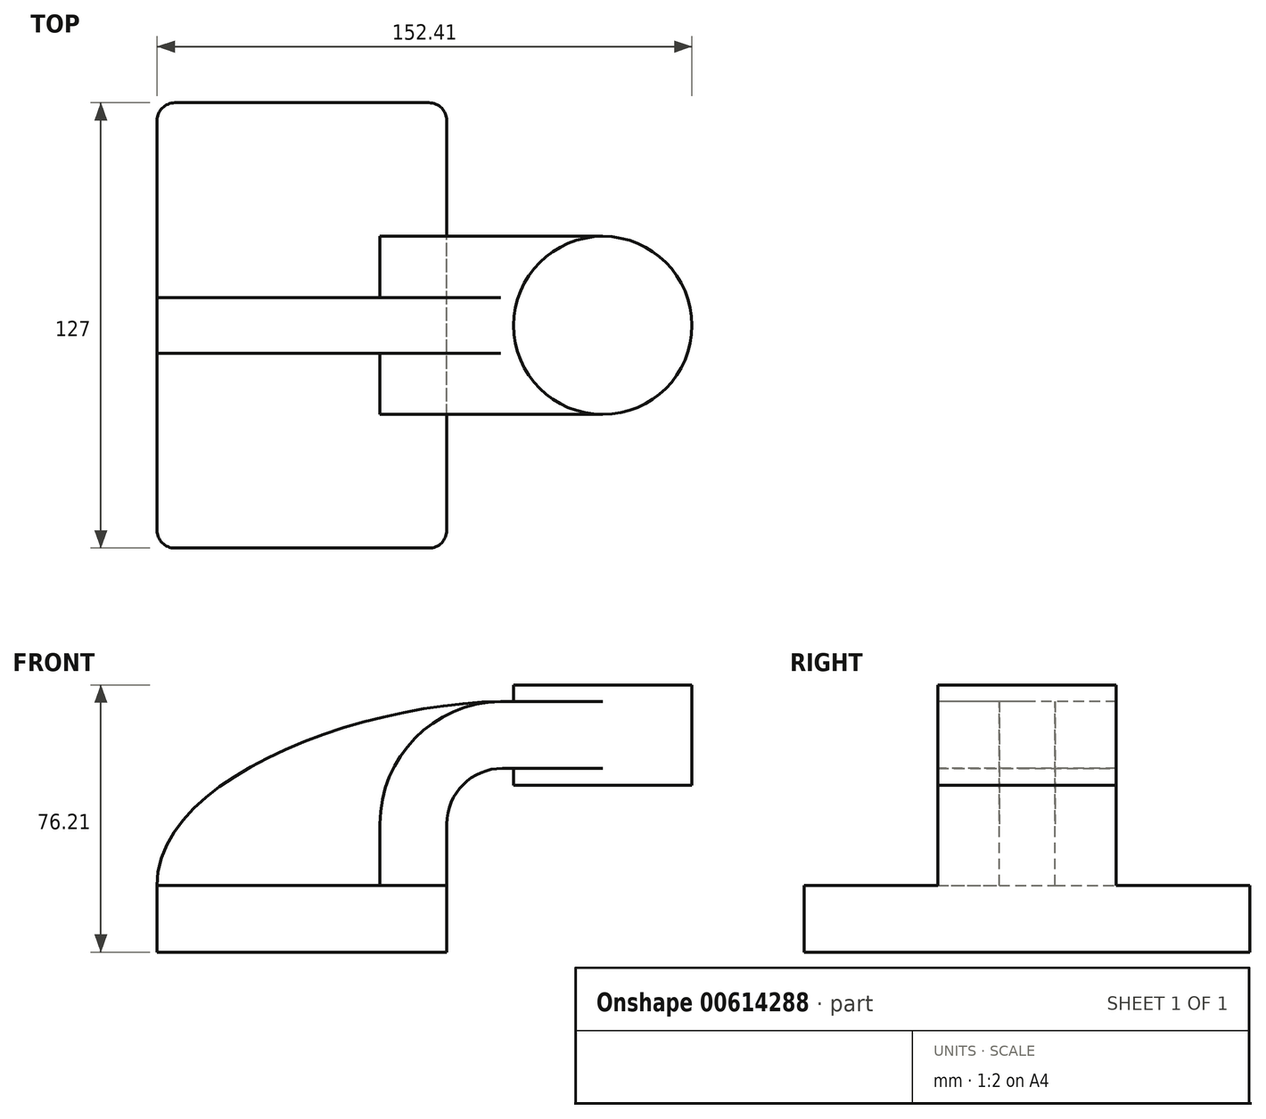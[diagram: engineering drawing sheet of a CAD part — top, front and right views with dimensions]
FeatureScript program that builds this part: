
annotation { "Feature Type Name" : "Feature", "Feature Type Description" : "" }
export const myFeature = defineFeature(function(context is Context, id is Id, definition is map)
    precondition{}
    {
        {
            var Q0;
            Q0=qCreatedBy(makeId("Front.planeOp"),FACE);
            var sketch = newSketch(context, id + "F0", { "sketchPlane" : qUnion([Q0])});
            skLineSegment(sketch, "E0.bottom", {"start": v(-41.28, 9.52) * mm, "end": v(41.27, 9.53) * mm});
            skLineSegment(sketch, "E0.top", {"start": v(-41.27, -9.53) * mm, "end": v(41.28, -9.53) * mm});
            skLineSegment(sketch, "E0.left", {"start": v(-41.28, 9.52) * mm, "end": v(-41.27, -9.53) * mm});
            skLineSegment(sketch, "E0.right", {"start": v(41.28, 9.53) * mm, "end": v(41.28, -9.52) * mm});
            skPoint(sketch, "E0.middle", {"position": v(0, 0) * mm});
            skLineSegment(sketch, "E1.bottom", {"start": v(60.32, 38.1) * mm, "end": v(111.12, 38.1) * mm});
            skLineSegment(sketch, "E1.top", {"start": v(60.32, 66.67) * mm, "end": v(111.12, 66.67) * mm});
            skLineSegment(sketch, "E1.left", {"start": v(60.32, 38.1) * mm, "end": v(60.32, 66.68) * mm});
            skLineSegment(sketch, "E1.right", {"start": v(111.12, 38.1) * mm, "end": v(111.12, 66.68) * mm});
            skPoint(sketch, "E1.middle", {"position": v(85.72, 52.39) * mm});
            skLineSegment(sketch, "E2", {"start": v(41.28, 9.53) * mm, "end": v(41.28, 27) * mm});
            skLineSegment(sketch, "E3", {"start": v(85.72, 38.1) * mm, "end": v(85.72, 66.67) * mm});
            skArc(sketch, "E4", {"start": v(41.27, 27) * mm, "mid": v(45.92, 38.23) * mm, "end": v(57.15, 42.88) * mm});
            skLineSegment(sketch, "E5", {"start": v(57.15, 42.88) * mm, "end": v(85.72, 42.88) * mm});
            skLineSegment(sketch, "E6.0", {"start": v(57.15, 61.93) * mm, "end": v(85.72, 61.93) * mm});
            skArc(sketch, "E6.1", {"start": v(22.23, 27) * mm, "mid": v(32.45, 51.7) * mm, "end": v(57.15, 61.93) * mm});
            skLineSegment(sketch, "E6.2", {"start": v(22.22, 9.53) * mm, "end": v(22.22, 27) * mm});
            skFitSpline(sketch, "E7", {"points": [v(-41.28, 9.52) * mm, v(57.15, 61.93) * mm], "startDerivative": vector(-1.16, 92.37) * mm, "endDerivative": vector(118.25, 0.68) * mm});
            skSolve(sketch);
        }
        {
            var Q0;
            Q0=makeQuery(id+"F0.imprint","IMPRINT",FACE,{"disambiguationData":[TD([[makeQuery(id+"F0.imprint","IMPRINT",EDGE,{"derivedFrom":sQuery(id+"F0.wireOp",EDGE,"E0.top")}),1.0]])]});
            extrude(context, id + "F1", {"entities" : qUnion([Q0]), "endBound" : BoundingType.SYMMETRIC, "depth" : 127 * mm, "offsetDistance" : 25.4 * mm});
        }
        {
            var Q0;
            {var subQ3=sQuery(id+"F0.wireOp",EDGE,"e5b6676b-119b-4408-bcbb-25903c91cb7e.2");Q0=makeQuery(id+"F0.imprint","IMPRINT",FACE,{"disambiguationData":[TD([[makeQuery(id+"F0.imprint","IMPRINT",EDGE,{"derivedFrom":subQ3}),1.0]])]});}
            var Q1;
            {var subQ3=sQuery(id+"F0.wireOp",EDGE,"E6.2");Q1=makeQuery(id+"F0.imprint","IMPRINT",FACE,{"disambiguationData":[TD([[makeQuery(id+"F0.imprint","IMPRINT",EDGE,{"derivedFrom":subQ3}),1.0]])]});}
            extrude(context, id + "F2", {"entities" : qUnion([Q0, Q1]), "operationType" : NewBodyOperationType.ADD, "endBound" : BoundingType.SYMMETRIC, "depth" : 15.88 * mm, "offsetDistance" : 25.4 * mm});
        }
        {
            var Q0;
            {var subQ0=sQuery(id+"F0.wireOp",EDGE,"E2");Q0=makeQuery(id+"F0.imprint","IMPRINT",FACE,{"disambiguationData":[TD([[makeQuery(id+"F0.imprint","IMPRINT",EDGE,{"derivedFrom":subQ0}),1.0]])]});}
            extrude(context, id + "F3", {"entities" : qUnion([Q0]), "operationType" : NewBodyOperationType.ADD, "endBound" : BoundingType.SYMMETRIC, "depth" : 50.8 * mm, "offsetDistance" : 25.4 * mm});
        }
        {
            var Q0;
            {var subQ0=sQuery(id+"F0.wireOp",EDGE,"E5");var subQ1=sQuery(id+"F0.wireOp",EDGE,"E1.left");var subQ2=makeQuery(id+"F0.imprint","INTERSECT",VERTEX,{"derivedFrom":[subQ1,subQ0]});Q0=makeQuery(id+"F0.imprint","IMPRINT",FACE,{"disambiguationData":[TD([[makeQuery(id+"F0.imprint","IMPRINT",EDGE,{"disambiguationData":[TD([[subQ2,-1.0]])],"derivedFrom":subQ1}),-1.0]])]});}
            extrude(context, id + "F4", {"entities" : qUnion([Q0]), "operationType" : NewBodyOperationType.ADD, "endBound" : BoundingType.SYMMETRIC, "depth" : 50.8 * mm, "offsetDistance" : 25.4 * mm});
        }
        {
            var Q0;
            {var subQ4=sQuery(id+"F0.wireOp",EDGE,"E1.right");Q0=makeQuery(id+"F0.imprint","IMPRINT",FACE,{"disambiguationData":[TD([[makeQuery(id+"F0.imprint","IMPRINT",EDGE,{"derivedFrom":subQ4}),1.0]])]});}
            var Q1;
            Q1=sQuery(id+"F0.wireOp",EDGE,"E3");
            revolve(context, id + "F5", {"operationType" : NewBodyOperationType.ADD, "entities" : qUnion([Q0]), "axis" : qUnion([Q1]), "revolveType" : RevolveType.FULL});
        }
        {
            var Q0;
            Q0=makeQuery(id+"F1.opExtrude","CAP_EDGE",EDGE,{"disambiguationData":[OSD([sQuery(id+"F0.wireOp",EDGE,"E0.left")])],"isStart":false});
            var Q1;
            Q1=makeQuery(id+"F1.opExtrude","CAP_EDGE",EDGE,{"disambiguationData":[OSD([sQuery(id+"F0.wireOp",EDGE,"E0.right")])],"isStart":false});
            var Q2;
            Q2=makeQuery(id+"F1.opExtrude","CAP_EDGE",EDGE,{"disambiguationData":[OSD([sQuery(id+"F0.wireOp",EDGE,"E0.right")])],"isStart":true});
            var Q3;
            Q3=makeQuery(id+"F1.opExtrude","CAP_EDGE",EDGE,{"disambiguationData":[OSD([sQuery(id+"F0.wireOp",EDGE,"E0.left")])],"isStart":true});
            fillet(context, id + "F6", {"entities" : qUnion([Q0, Q1, Q2, Q3]), "radius" : 5.08 * mm, "tangentPropagation" : true, "allowEdgeOverflow" : false});
        }
    });
